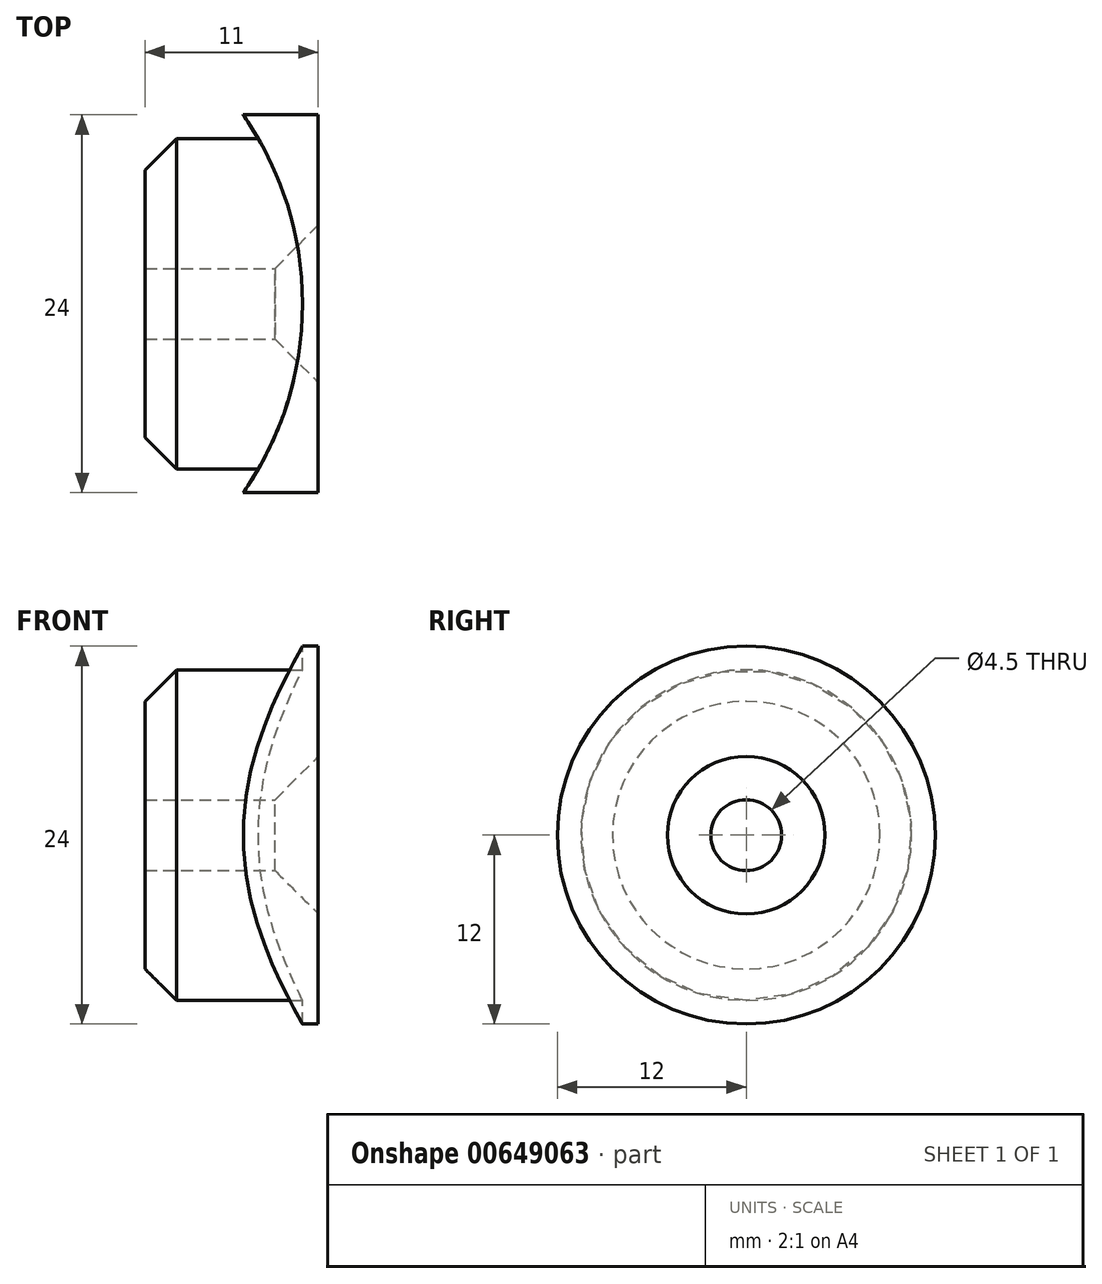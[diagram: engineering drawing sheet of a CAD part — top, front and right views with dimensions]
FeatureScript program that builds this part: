
annotation { "Feature Type Name" : "Feature", "Feature Type Description" : "" }
export const myFeature = defineFeature(function(context is Context, id is Id, definition is map)
    precondition{}
    {
        {
            var Q0;
            Q0=qCreatedBy(makeId("Right.planeOp"),FACE);
            var sketch = newSketch(context, id + "F0", { "sketchPlane" : qUnion([Q0])});
            skCircle(sketch, "E0", {"center": v(0, 0) * mm, "radius": 12 * mm});
            skSolve(sketch);
        }
        {
            var Q0;
            Q0=makeQuery(id+"F0.imprint","IMPRINT",FACE,{"disambiguationData":[TD([[makeQuery(id+"F0.imprint","IMPRINT",EDGE,{"derivedFrom":sQuery(id+"F0.wireOp",EDGE,"E0")}),1.0]])]});
            extrude(context, id + "F1", {"entities" : qUnion([Q0]), "depth" : 5 * mm, "offsetDistance" : 25 * mm});
        }
        {
            var Q0;
            Q0=qCreatedBy(makeId("Top.planeOp"),FACE);
            var sketch = newSketch(context, id + "F2", { "sketchPlane" : qUnion([Q0])});
            skCircle(sketch, "E1", {"center": v(-17, 0) * mm, "radius": 21 * mm});
            skSolve(sketch);
        }
        {
            var Q0;
            Q0=makeQuery(id+"F2.imprint","IMPRINT",FACE,{"disambiguationData":[TD([[makeQuery(id+"F2.imprint","IMPRINT",EDGE,{"derivedFrom":sQuery(id+"F2.wireOp",EDGE,"E1")}),1.0]])]});
            extrude(context, id + "F3", {"entities" : qUnion([Q0]), "operationType" : NewBodyOperationType.REMOVE, "endBound" : BoundingType.THROUGH_ALL, "oppositeDirection" : true, "depth" : 25 * mm, "offsetDistance" : 25 * mm, "hasSecondDirection" : true, "secondDirectionBound" : SecondDirectionBoundingType.THROUGH_ALL, "secondDirectionOppositeDirection" : false, "secondDirectionDepth" : 25 * mm});
        }
        {
            var Q0;
            Q0=qCreatedBy(makeId("Right.planeOp"),FACE);
            var sketch = newSketch(context, id + "F4", { "sketchPlane" : qUnion([Q0])});
            skCircle(sketch, "E2", {"center": v(0, 0) * mm, "radius": 10.5 * mm});
            skSolve(sketch);
        }
        {
            var Q0;
            Q0 = qSketchRegion(id + "F4", true);
            extrude(context, id + "F5", {"entities" : qUnion([Q0]), "operationType" : NewBodyOperationType.ADD, "oppositeDirection" : true, "depth" : 6 * mm, "offsetDistance" : 25 * mm, "hasSecondDirection" : true, "secondDirectionBound" : SecondDirectionBoundingType.UP_TO_NEXT, "secondDirectionOppositeDirection" : false, "secondDirectionDepth" : 25 * mm});
        }
        {
            var Q0;
            Q0=makeQuery(id+"F5.opExtrude","CAP_EDGE",EDGE,{"disambiguationData":[OSD([sQuery(id+"F4.wireOp",EDGE,"E2")])],"isStart":false});
            chamfer(context, id + "F6", {"entities" : qUnion([Q0]), "width" : 2 * mm, "tangentPropagation" : true});
        }
        {
            var Q0;
            Q0=makeQuery(id+"F1.opExtrude","CAP_FACE",FACE,{"disambiguationData":[OSD([sQuery(id+"F0.wireOp",EDGE,"E0")])],"isStart":false});
            var sketch = newSketch(context, id + "F7", { "sketchPlane" : qUnion([Q0])});
            skPoint(sketch, "E3", {"position": v(0, 0) * mm});
            skSolve(sketch);
        }
        {
            var Q0;
            Q0=sQuery(id+"F7.wireOp",VERTEX,"E3");
            var Q1;
            Q1=makeQuery(id+"F1.opExtrude","SWEPT_BODY",BODY,{"disambiguationData":[OSD([sQuery(id+"F0.wireOp",EDGE,"E0")])]});
            hole(context, id + "F8", {"style" : HoleStyle.C_SINK, "endStyle" : HoleEndStyle.THROUGH, "holeDiameter" : 4.5 * mm, "cSinkDiameter" : 10 * mm, "cSinkAngle" : 90 * degree, "majorDiameter" : 5 * mm, "isTappedThrough" : true, "tappedDepth" : 12 * mm, "tapClearance" : 3, "locations" : qUnion([Q0]), "scope" : qUnion([Q1])});
        }
    });
